# Revit family: Protek Q2
name_source: partatom
category: Luminarias
revit_build: Autodesk Revit 2015 (Build: 20140606_1530(x64)
units: mm (PartAtom-declared; Revit-internal decimal feet)

## types (16) — shared parameters
Anchura rectángulo de emisión = 290 mm  [stored 0.951444 ft]
Cambio de temperatura de color de luz atenuada = <Ninguno>
Fabricante = SECOM ILUMINACIÓN
Filtro de color = 16777215
Forma visible en renderización = No
Longitud de rectángulo de emisión = 222 mm
Lámpara = LED Osram Oslon SLL
Modelo = Protek Q2
Ángulo de inclinación = 90.00°

## per-type parameters (varying)
| type | Archivo de red fotométrica | Comentarios de vataje | Descripción | Óptica angulo de apertura |
| Protek Q2 60W/ 80º | 4330 02 60 84 (80º).IES | 60W | 4330 01 60 84 | 80.00° |
| Protek Q2 100 W / 80º | 4330 02 10 84 (80º).IES | 100W | 4330 01 10 84 | 80.00° |
| Protek Q2 150W / 80º | 4330 02 15 84 (80º).IES | 150W | 4330 01 15 84 | 80.00° |
| Protek Q2 200W / 80º | 4330 02 20 84 (80º).IES | 200W | 4330 01 20 84 | 80.00° |
| Protek Q2 60W / 48º | 4330 02 60 84 3409 (48º).IES | 60W | 4330 01 60 84 3409 | 48.00° |
| Protek Q2 100W / 48º | 4330 02 10 84 3409 (48º).IES | 100W | 4330 01 10 84 3409 | 48.00° |
| Protek Q2 150w / 48º | 4330 02 15 84 3409 (48º).IES | 150W | 4330 01 15 84 3409 | 48.00° |
| Protek Q2 200W / 48º | 4330 02 20 84 3409 (48º).IES | 200W | 4330 01 20 84 3409 | 48.00° |
| Protek Q2 60W / 150º | 4330 02 60 84 3421 (150º) C7.IES | 60W | 4330 01 60 84 3421 | 150.00° |
| Protek Q2 100W / 150º | 4330 02 10 84 3421 (150º) C7.IES | 100W | 4330 01 10 84 3421 | 150.00° |
| Protek Q2 150W / 150º | 4330 02 15 84 3421 (150º) C7.IES | 150W | 4330 01 15 84 3421 | 48.00° |
| Protek Q2 200W / 150º | 4330 02 20 84 3421 (150º) C7.IES | 200W | 4330 01 20 84 3421 | 150.00° |
| Protek Q2 60W / Asimétrica 150º | 4330 02 60 84 3407.IES | 60W | 4330 01 60 84 3407 3421 | 150.00° |
| Protek Q2 100W / Asimétrica 150º | 4330 02 10 84 3407.IES | 100W | 4330 01 10 84 3407 3421 | 150.00° |
| Protek Q2 150W / Asimétrica 150º | 4330 02 15 84 3407.IES | 150W | 4330 01 15 84 3407 3421 | 48.00° |
| Protek Q2 200W / Asimétrica 150º | 4330 02 20 84 3407.IES | 200W | 4330 01 20 84 3407 3421 | 150.00° |

note: [stored X ft] marks values corroborated as IEEE doubles in the binary element streams (Revit-internal decimal feet)
